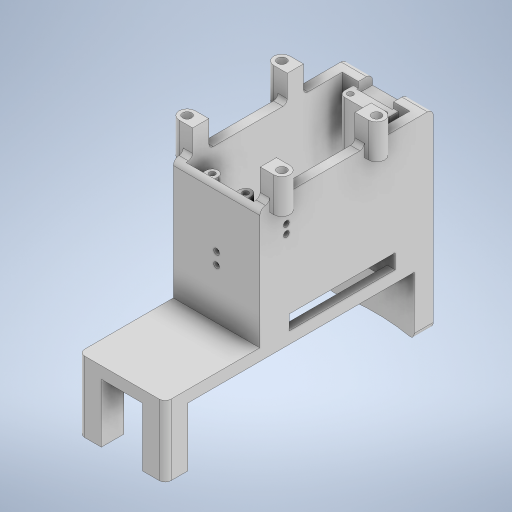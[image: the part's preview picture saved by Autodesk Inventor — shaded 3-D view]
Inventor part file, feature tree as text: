
AUTODESK INVENTOR PART (.ipt)
format: ipt  version: 2023 (Build 270158000, 158)  size: 535,040 bytes
history: native  units: mm
features: extrude x13, sketch x10, other x4, fillet x4
ambient origin geometry x8: Origin, YZ Plane, XZ Plane, XY Plane, X Axis, Y Axis, Z Axis, Center Point
bodies: Body1 (feature_tree)
feature tree (31):
  other  "断面1"
  other  "断面2"
  other  "断面3"
  other  "ソリッド1"
  sketch  "スケッチ1"
  extrude  "押し出し1"  Depth=29.4mm
  extrude  "押し出し2"  Depth=14.0mm
  extrude  "押し出し3"  Depth=5.0mm
  sketch  "スケッチ3"
  extrude  "押し出し4"  Depth=1.5mm
  extrude  "押し出し5"  Depth=78.5mm
  sketch  "スケッチ7"
  extrude  "押し出し11"  Depth=36.0mm
  extrude  "押し出し12"  Depth=24.0mm
  extrude  "押し出し13"  Depth=20.0mm TaperAngle=0.0deg
  extrude  "押し出し14"  Depth=4.0mm TaperAngle=0.0deg
  extrude  "押し出し16"  Depth=10.0mm
  extrude  "押し出し17"  Depth=5.0mm TaperAngle=0.0deg
  extrude  "押し出し22"  Depth=12.5mm
  fillet  "フィレット7"  Radius=4.5mm
  fillet  "フィレット8"  Radius=4.5mm
  fillet  "フィレット6"  Radius=2.8mm
  fillet  "フィレット9"  Radius=13.0mm
  extrude  "押し出し23"  Depth=2.0mm
  sketch  "スケッチ2"
  sketch  "スケッチ8"
  sketch  "スケッチ9"
  sketch  "スケッチ11"
  sketch  "スケッチ12"
  sketch  "スケッチ17"
  sketch  "スケッチ18"
